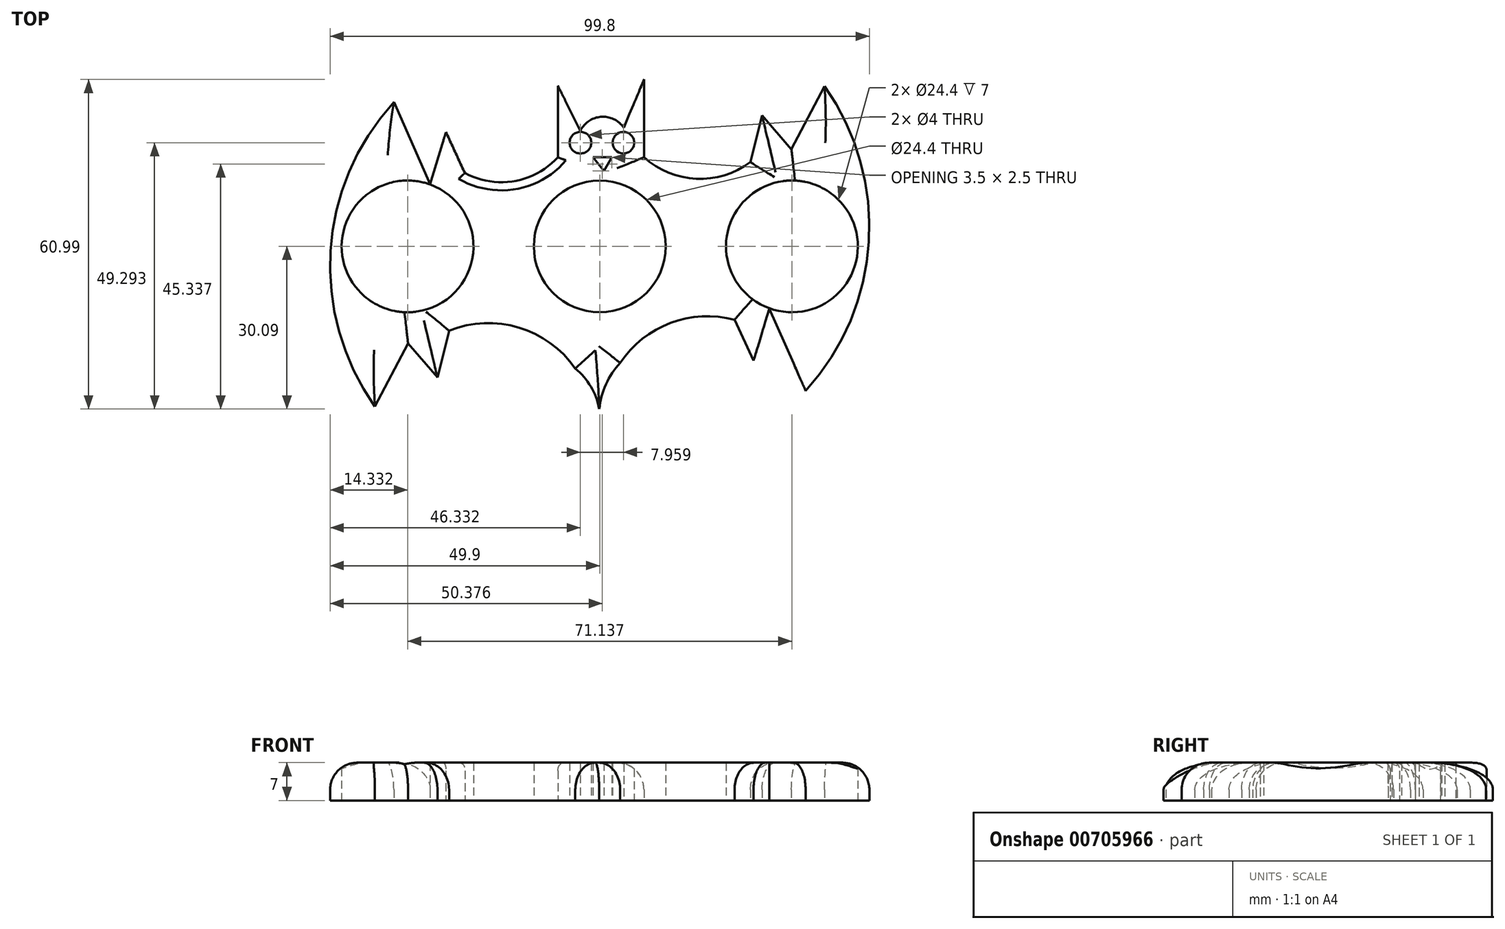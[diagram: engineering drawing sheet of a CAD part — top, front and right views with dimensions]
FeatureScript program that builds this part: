
annotation { "Feature Type Name" : "Feature", "Feature Type Description" : "" }
export const myFeature = defineFeature(function(context is Context, id is Id, definition is map)
    precondition{}
    {
        {
            var Q0;
            Q0=qCreatedBy(makeId("Top.planeOp"),FACE);
            var sketch = newSketch(context, id + "F0", { "sketchPlane" : qUnion([Q0])});
            skCircle(sketch, "E0", {"center": v(0, 0) * mm, "radius": 12.2 * mm});
            skArc(sketch, "E1", {"start": v(-38.1, 26.72) * mm, "mid": v(-49.82, -0.84) * mm, "end": v(-41.61, -29.64) * mm});
            skArc(sketch, "E2.1.0", {"start": v(38.1, -26.72) * mm, "mid": v(49.82, 0.84) * mm, "end": v(41.61, 29.64) * mm});
            skLineSegment(sketch, "E3", {"start": v(-41.61, -29.64) * mm, "end": v(-35.48, -17.96) * mm});
            skLineSegment(sketch, "E4", {"start": v(-35.48, -17.96) * mm, "end": v(-35.48, -24.97) * mm});
            skArc(sketch, "E5", {"start": v(-4.53, -22.63) * mm, "mid": v(-14.98, -15.03) * mm, "end": v(-27.89, -15.62) * mm});
            skLineSegment(sketch, "E6.1.0", {"start": v(41.61, 29.64) * mm, "end": v(35.48, 17.96) * mm});
            skLineSegment(sketch, "E6.1.1", {"start": v(35.48, 17.96) * mm, "end": v(30.03, 24.29) * mm});
            skLineSegment(sketch, "E6.1.2", {"start": v(30.03, 24.29) * mm, "end": v(27.89, 15.62) * mm});
            skLineSegment(sketch, "E7", {"start": v(38.1, -26.72) * mm, "end": v(31.4, -11.53) * mm});
            skLineSegment(sketch, "E8", {"start": v(31.4, -11.53) * mm, "end": v(28.47, -21.17) * mm});
            skLineSegment(sketch, "E9", {"start": v(28.47, -21.17) * mm, "end": v(24.97, -13.58) * mm});
            skArc(sketch, "E10.1.0", {"start": v(-24.97, 13.58) * mm, "mid": v(-15.85, 12.08) * mm, "end": v(-7.74, 16.5) * mm});
            skLineSegment(sketch, "E10.1.2", {"start": v(-28.47, 21.17) * mm, "end": v(-24.97, 13.58) * mm});
            skLineSegment(sketch, "E10.1.4", {"start": v(-31.4, 11.53) * mm, "end": v(-28.47, 21.17) * mm});
            skLineSegment(sketch, "E10.1.5", {"start": v(-38.1, 26.72) * mm, "end": v(-31.4, 11.53) * mm});
            skArc(sketch, "E11", {"start": v(0, -34.06) * mm, "mid": v(-0.76, -27.75) * mm, "end": v(-4.53, -22.63) * mm});
            skArc(sketch, "E12.1.0", {"start": v(8.2, 16.53) * mm, "mid": v(17.88, 12.52) * mm, "end": v(27.89, 15.62) * mm});
            skLineSegment(sketch, "E13", {"start": v(-7.74, 16.5) * mm, "end": v(-7.74, 29.75) * mm});
            skLineSegment(sketch, "E14", {"start": v(-7.74, 29.75) * mm, "end": v(-3.6, 21.41) * mm});
            skLineSegment(sketch, "E15", {"start": v(8.2, 16.53) * mm, "end": v(8.2, 30.9) * mm});
            skLineSegment(sketch, "E16", {"start": v(8.2, 30.9) * mm, "end": v(4.45, 21.97) * mm});
            skArc(sketch, "E17", {"start": v(4.45, 21.97) * mm, "mid": v(0.27, 24) * mm, "end": v(-3.6, 21.41) * mm});
            skArc(sketch, "E18", {"start": v(24.97, -13.58) * mm, "mid": v(13.1, -14.2) * mm, "end": v(3.78, -21.57) * mm});
            skArc(sketch, "E19", {"start": v(3.78, -21.57) * mm, "mid": v(0.47, -27.38) * mm, "end": v(0, -34.06) * mm});
            skLineSegment(sketch, "E20.1.0", {"start": v(-35.48, -17.96) * mm, "end": v(-30.03, -24.29) * mm});
            skLineSegment(sketch, "E20.1.1", {"start": v(-30.03, -24.29) * mm, "end": v(-27.89, -15.62) * mm});
            skCircle(sketch, "E21", {"center": v(35.57, 0) * mm, "radius": 12.2 * mm});
            skCircle(sketch, "E22", {"center": v(-35.57, 0) * mm, "radius": 12.2 * mm});
            skCircle(sketch, "E23", {"center": v(-3.57, 19.2) * mm, "radius": 1 * mm});
            skCircle(sketch, "E24", {"center": v(4.4, 19.2) * mm, "radius": 1 * mm});
            skCircle(sketch, "E25", {"center": v(-3.57, 19.2) * mm, "radius": 2 * mm});
            skCircle(sketch, "E26", {"center": v(4.4, 19.2) * mm, "radius": 2 * mm});
            skPoint(sketch, "E27.0.internal.orphan", {"position": v(-1.27, 16.5) * mm});
            skPoint(sketch, "E27.1.internal.orphan", {"position": v(2.23, 16.5) * mm});
            skPoint(sketch, "E28.end.orphan", {"position": v(2.23, 15.54) * mm});
            skLineSegment(sketch, "E29", {"start": v(-1.27, 16.5) * mm, "end": v(2.23, 16.5) * mm});
            skLineSegment(sketch, "E30", {"start": v(2.23, 16.5) * mm, "end": v(0.79, 14) * mm});
            skLineSegment(sketch, "E31", {"start": v(-1.27, 16.5) * mm, "end": v(0.79, 14) * mm});
            skSolve(sketch);
        }
        {
            var Q0;
            Q0=makeQuery(id+"F0.imprint","IMPRINT",FACE,{"disambiguationData":[TD([[makeQuery(id+"F0.imprint","IMPRINT",EDGE,{"derivedFrom":sQuery(id+"F0.wireOp",EDGE,"E0")}),-1.0]])]});
            var Q1;
            Q1=makeQuery(id+"F0.imprint","IMPRINT",FACE,{"disambiguationData":[TD([[makeQuery(id+"F0.imprint","IMPRINT",EDGE,{"derivedFrom":sQuery(id+"F0.wireOp",EDGE,"6iGZHZtX-1bip-HH5F-Ro9x-hsKvWLjZBWyp")}),-1.0]])]});
            extrude(context, id + "F1", {"entities" : qUnion([Q0, Q1]), "depth" : 7 * mm, "offsetDistance" : 25 * mm});
        }
        {
            var Q0;
            Q0=makeQuery(id+"F1.opExtrude","CAP_EDGE",EDGE,{"disambiguationData":[OSD([sQuery(id+"F0.wireOp",EDGE,"E10.1.2")])],"isStart":false});
            var Q1;
            Q1=makeQuery(id+"F1.opExtrude","CAP_EDGE",EDGE,{"disambiguationData":[OSD([sQuery(id+"F0.wireOp",EDGE,"E10.1.0")])],"isStart":false});
            var Q2;
            Q2=makeQuery(id+"F1.opExtrude","CAP_EDGE",EDGE,{"disambiguationData":[OSD([sQuery(id+"F0.wireOp",EDGE,"E13")])],"isStart":false});
            fillet(context, id + "F2", {"entities" : qUnion([Q0, Q1, Q2]), "radius" : 1.5 * mm, "tangentPropagation" : true, "rho" : 0.5, "crossSection" : FilletCrossSection.CONIC, "allowEdgeOverflow" : false});
        }
        {
            var Q0;
            Q0=makeQuery(id+"F1.opExtrude","CAP_EDGE",EDGE,{"disambiguationData":[OSD([sQuery(id+"F0.wireOp",EDGE,"E10.1.5")])],"isStart":false});
            var Q1;
            Q1=makeQuery(id+"F1.opExtrude","CAP_EDGE",EDGE,{"disambiguationData":[OSD([sQuery(id+"F0.wireOp",EDGE,"E1")])],"isStart":false});
            var Q2;
            Q2=makeQuery(id+"F1.opExtrude","CAP_EDGE",EDGE,{"disambiguationData":[OSD([sQuery(id+"F0.wireOp",EDGE,"E3")])],"isStart":false});
            var Q3;
            Q3=makeQuery(id+"F1.opExtrude","CAP_EDGE",EDGE,{"disambiguationData":[OSD([sQuery(id+"F0.wireOp",EDGE,"E20.1.0")])],"isStart":false});
            var Q4;
            Q4=makeQuery(id+"F1.opExtrude","CAP_EDGE",EDGE,{"disambiguationData":[OSD([sQuery(id+"F0.wireOp",EDGE,"E5")])],"isStart":false});
            var Q5;
            Q5=makeQuery(id+"F1.opExtrude","CAP_EDGE",EDGE,{"disambiguationData":[OSD([sQuery(id+"F0.wireOp",EDGE,"E20.1.1")])],"isStart":false});
            var Q6;
            Q6=makeQuery(id+"F1.opExtrude","CAP_EDGE",EDGE,{"disambiguationData":[OSD([sQuery(id+"F0.wireOp",EDGE,"E11")])],"isStart":false});
            var Q7;
            Q7=makeQuery(id+"F1.opExtrude","CAP_EDGE",EDGE,{"disambiguationData":[OSD([sQuery(id+"F0.wireOp",EDGE,"E18")])],"isStart":false});
            var Q8;
            Q8=makeQuery(id+"F1.opExtrude","CAP_EDGE",EDGE,{"disambiguationData":[OSD([sQuery(id+"F0.wireOp",EDGE,"E19")])],"isStart":false});
            var Q9;
            Q9=makeQuery(id+"F1.opExtrude","CAP_EDGE",EDGE,{"disambiguationData":[OSD([sQuery(id+"F0.wireOp",EDGE,"E9")])],"isStart":false});
            fillet(context, id + "F3", {"entities" : qUnion([Q0, Q1, Q2, Q3, Q4, Q5, Q6, Q7, Q8, Q9]), "radius" : 5 * mm, "tangentPropagation" : true, "allowEdgeOverflow" : false});
        }
        {
            var Q0;
            Q0=makeQuery(id+"F1.opExtrude","CAP_EDGE",EDGE,{"disambiguationData":[OSD([sQuery(id+"F0.wireOp",EDGE,"E2.1.0")])],"isStart":false});
            var Q1;
            Q1=makeQuery(id+"F1.opExtrude","CAP_EDGE",EDGE,{"disambiguationData":[OSD([sQuery(id+"F0.wireOp",EDGE,"E6.1.0")])],"isStart":false});
            var Q2;
            Q2=makeQuery(id+"F1.opExtrude","CAP_EDGE",EDGE,{"disambiguationData":[OSD([sQuery(id+"F0.wireOp",EDGE,"E6.1.1")])],"isStart":false});
            var Q3;
            Q3=makeQuery(id+"F1.opExtrude","CAP_EDGE",EDGE,{"disambiguationData":[OSD([sQuery(id+"F0.wireOp",EDGE,"E12.1.0")])],"isStart":false});
            var Q4;
            Q4=makeQuery(id+"F1.opExtrude","CAP_EDGE",EDGE,{"disambiguationData":[OSD([sQuery(id+"F0.wireOp",EDGE,"E6.1.2")])],"isStart":false});
            var Q5;
            Q5=makeQuery(id+"F1.opExtrude","CAP_EDGE",EDGE,{"disambiguationData":[OSD([sQuery(id+"F0.wireOp",EDGE,"E15")])],"isStart":false});
            fillet(context, id + "F4", {"entities" : qUnion([Q0, Q1, Q2, Q3, Q4, Q5]), "radius" : 5 * mm, "tangentPropagation" : true, "allowEdgeOverflow" : false});
        }
    });
